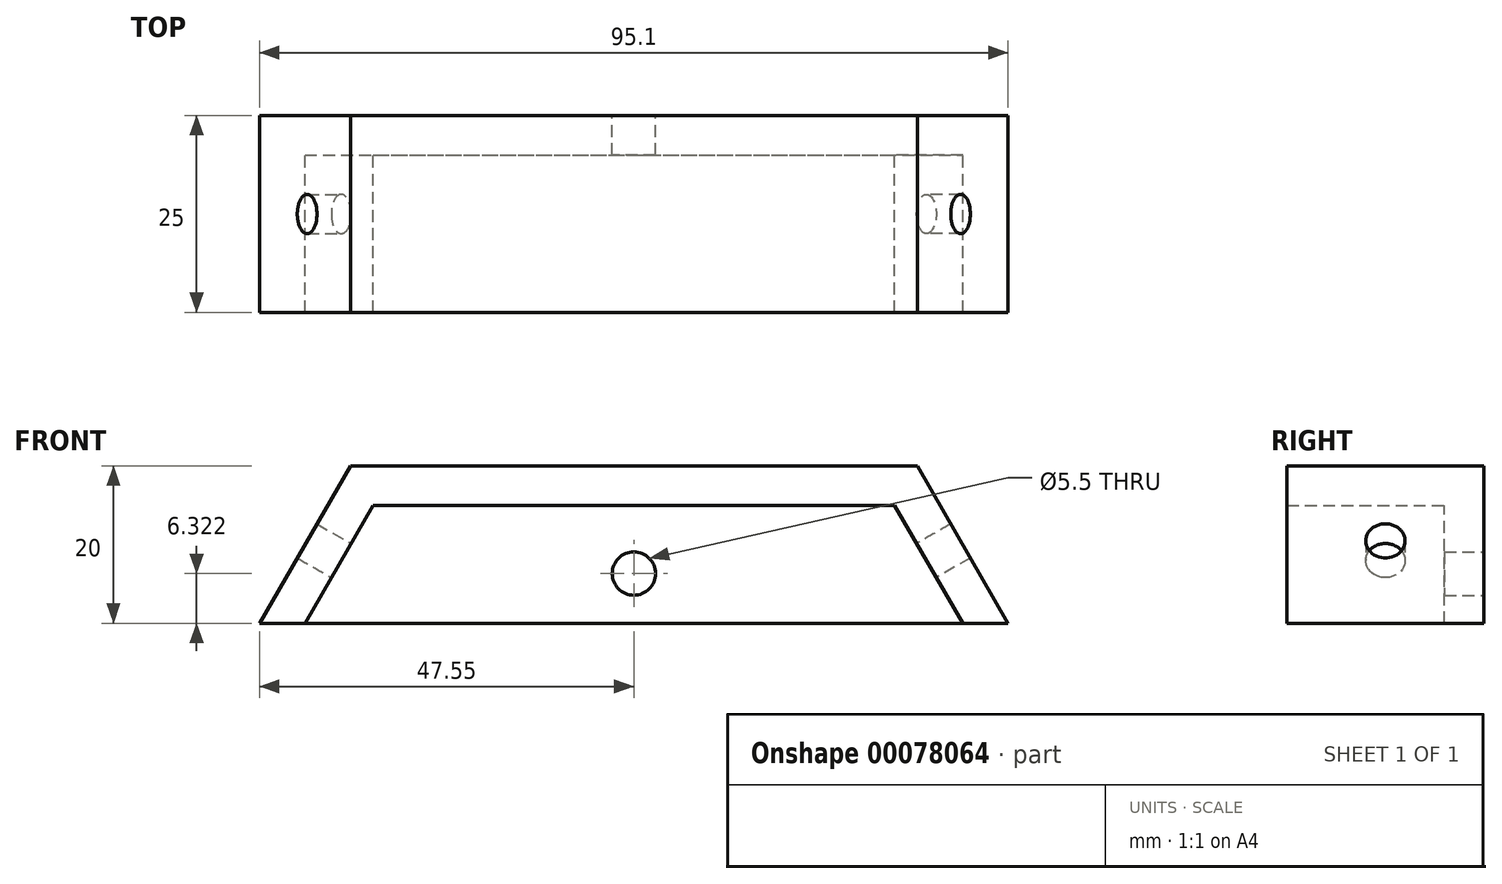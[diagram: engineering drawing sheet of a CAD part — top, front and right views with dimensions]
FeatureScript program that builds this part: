
annotation { "Feature Type Name" : "Feature", "Feature Type Description" : "" }
export const myFeature = defineFeature(function(context is Context, id is Id, definition is map)
    precondition{}
    {
        {
            var Q0;
            Q0=qCreatedBy(makeId("Front.planeOp"),FACE);
            var sketch = newSketch(context, id + "F0", { "sketchPlane" : qUnion([Q0])});
            skLineSegment(sketch, "E0", {"start": v(0, 0) * mm, "end": v(36, 0) * mm});
            skLineSegment(sketch, "E1", {"start": v(36, 0) * mm, "end": v(47.55, -20) * mm});
            skLineSegment(sketch, "E2", {"start": v(47.55, -20) * mm, "end": v(0, -20) * mm});
            skLineSegment(sketch, "E3.MirrorCS", {"start": v(-47.55, -20) * mm, "end": v(0, -20) * mm});
            skLineSegment(sketch, "E4.MirrorCS", {"start": v(0, 0) * mm, "end": v(-36, 0) * mm});
            skLineSegment(sketch, "E5.MirrorCS", {"start": v(-36, 0) * mm, "end": v(-47.55, -20) * mm});
            skSolve(sketch);
        }
        {
            var Q0;
            Q0 = qSketchRegion(id + "F0", true);
            extrude(context, id + "F1", {"entities" : qUnion([Q0]), "depth" : 5 * mm, "offsetDistance" : 25 * mm});
        }
        {
            var Q0;
            Q0=makeQuery(id+"F1.opExtrude","CAP_FACE",FACE,{"disambiguationData":[OSD([sQuery(id+"F0.wireOp",EDGE,"E0"),sQuery(id+"F0.wireOp",EDGE,"E1"),sQuery(id+"F0.wireOp",EDGE,"E2"),sQuery(id+"F0.wireOp",EDGE,"E3.MirrorCS"),sQuery(id+"F0.wireOp",EDGE,"E4.MirrorCS"),sQuery(id+"F0.wireOp",EDGE,"E5.MirrorCS")])],"isStart":false});
            var sketch = newSketch(context, id + "F2", { "sketchPlane" : qUnion([Q0])});
            skLineSegment(sketch, "E6", {"start": v(-36, 0) * mm, "end": v(-47.55, -20) * mm});
            skLineSegment(sketch, "E7", {"start": v(36, 0) * mm, "end": v(47.55, -20) * mm});
            skLineSegment(sketch, "E8", {"start": v(-41.77, -20) * mm, "end": v(-30.23, 0) * mm});
            skLineSegment(sketch, "E9", {"start": v(41.77, -20) * mm, "end": v(30.23, 0) * mm});
            skLineSegment(sketch, "E10", {"start": v(-36, 0) * mm, "end": v(-30.23, 0) * mm});
            skLineSegment(sketch, "E11", {"start": v(-47.55, -20) * mm, "end": v(-41.77, -20) * mm});
            skLineSegment(sketch, "E12", {"start": v(41.77, -20) * mm, "end": v(47.55, -20) * mm});
            skLineSegment(sketch, "E13", {"start": v(30.23, 0) * mm, "end": v(36, 0) * mm});
            skLineSegment(sketch, "E14", {"start": v(-30.23, 0) * mm, "end": v(30.23, 0) * mm});
            skLineSegment(sketch, "E15", {"start": v(-33.11, -5) * mm, "end": v(33.11, -5) * mm});
            skSolve(sketch);
        }
        {
            var Q0;
            Q0 = qSketchRegion(id + "F2", true);
            extrude(context, id + "F3", {"entities" : qUnion([Q0]), "operationType" : NewBodyOperationType.ADD, "depth" : 20 * mm, "offsetDistance" : 25 * mm});
        }
        {
            var Q0;
            Q0=makeQuery(id+"F1.opExtrude","CAP_FACE",FACE,{"disambiguationData":[OSD([sQuery(id+"F0.wireOp",EDGE,"E0"),sQuery(id+"F0.wireOp",EDGE,"E1"),sQuery(id+"F0.wireOp",EDGE,"E2"),sQuery(id+"F0.wireOp",EDGE,"E3.MirrorCS"),sQuery(id+"F0.wireOp",EDGE,"E4.MirrorCS"),sQuery(id+"F0.wireOp",EDGE,"E5.MirrorCS")])],"isStart":false});
            var sketch = newSketch(context, id + "F4", { "sketchPlane" : qUnion([Q0])});
            skPoint(sketch, "E16", {"position": v(0, -13.68) * mm});
            skSolve(sketch);
        }
        {
            var Q0;
            Q0=sQuery(id+"F4.wireOp",VERTEX,"E16");
            var Q1;
            Q1=makeQuery(id+"F1.opExtrude","SWEPT_BODY",BODY,{"disambiguationData":[OSD([sQuery(id+"F0.wireOp",EDGE,"E0"),sQuery(id+"F0.wireOp",EDGE,"E1"),sQuery(id+"F0.wireOp",EDGE,"E2"),sQuery(id+"F0.wireOp",EDGE,"E3.MirrorCS"),sQuery(id+"F0.wireOp",EDGE,"E4.MirrorCS"),sQuery(id+"F0.wireOp",EDGE,"E5.MirrorCS")])]});
            hole(context, id + "F5", {"style" : HoleStyle.SIMPLE, "endStyle" : HoleEndStyle.THROUGH, "holeDiameter" : 5.5 * mm, "majorDiameter" : 5 * mm, "tappedDepth" : 12 * mm, "tapClearance" : 3, "locations" : qUnion([Q0]), "scope" : qUnion([Q1])});
        }
        {
            var Q0;
            Q0=makeQuery(id+"F3.boolean.opBoolean","MERGE",FACE,{"derivedFrom":[makeQuery(id+"F1.opExtrude","SWEPT_FACE",FACE,{"disambiguationData":[OSD([sQuery(id+"F0.wireOp",EDGE,"E1")])]}),makeQuery(id+"F3.opExtrude","SWEPT_FACE",FACE,{"disambiguationData":[OSD([sQuery(id+"F2.wireOp",EDGE,"E7")])]})]});
            var sketch = newSketch(context, id + "F6", { "sketchPlane" : qUnion([Q0])});
            skPoint(sketch, "E17", {"position": v(-12.5, -29) * mm});
            skSolve(sketch);
        }
        {
            var Q0;
            Q0=sQuery(id+"F6.wireOp",VERTEX,"E17");
            var Q1;
            Q1=makeQuery(id+"F1.opExtrude","SWEPT_BODY",BODY,{"disambiguationData":[OSD([sQuery(id+"F0.wireOp",EDGE,"E0"),sQuery(id+"F0.wireOp",EDGE,"E1"),sQuery(id+"F0.wireOp",EDGE,"E2"),sQuery(id+"F0.wireOp",EDGE,"E3.MirrorCS"),sQuery(id+"F0.wireOp",EDGE,"E4.MirrorCS"),sQuery(id+"F0.wireOp",EDGE,"E5.MirrorCS")])]});
            hole(context, id + "F7", {"style" : HoleStyle.SIMPLE, "endStyle" : HoleEndStyle.THROUGH, "holeDiameter" : 5 * mm, "majorDiameter" : 5 * mm, "tappedDepth" : 12 * mm, "tapClearance" : 3, "locations" : qUnion([Q0]), "scope" : qUnion([Q1])});
        }
        {
            var Q0;
            Q0=makeQuery(id+"F3.boolean.opBoolean","MERGE",FACE,{"derivedFrom":[makeQuery(id+"F1.opExtrude","SWEPT_FACE",FACE,{"disambiguationData":[OSD([sQuery(id+"F0.wireOp",EDGE,"E5.MirrorCS")])]}),makeQuery(id+"F3.opExtrude","SWEPT_FACE",FACE,{"disambiguationData":[OSD([sQuery(id+"F2.wireOp",EDGE,"E6")])]})]});
            var sketch = newSketch(context, id + "F8", { "sketchPlane" : qUnion([Q0])});
            skPoint(sketch, "E18", {"position": v(12.5, -29) * mm});
            skSolve(sketch);
        }
        {
            var Q0;
            Q0=sQuery(id+"F8.wireOp",VERTEX,"E18");
            var Q1;
            Q1=makeQuery(id+"F1.opExtrude","SWEPT_BODY",BODY,{"disambiguationData":[OSD([sQuery(id+"F0.wireOp",EDGE,"E0"),sQuery(id+"F0.wireOp",EDGE,"E1"),sQuery(id+"F0.wireOp",EDGE,"E2"),sQuery(id+"F0.wireOp",EDGE,"E3.MirrorCS"),sQuery(id+"F0.wireOp",EDGE,"E4.MirrorCS"),sQuery(id+"F0.wireOp",EDGE,"E5.MirrorCS")])]});
            hole(context, id + "F9", {"style" : HoleStyle.SIMPLE, "endStyle" : HoleEndStyle.THROUGH, "holeDiameter" : 5 * mm, "majorDiameter" : 5 * mm, "tappedDepth" : 12 * mm, "tapClearance" : 3, "locations" : qUnion([Q0]), "scope" : qUnion([Q1])});
        }
    });
